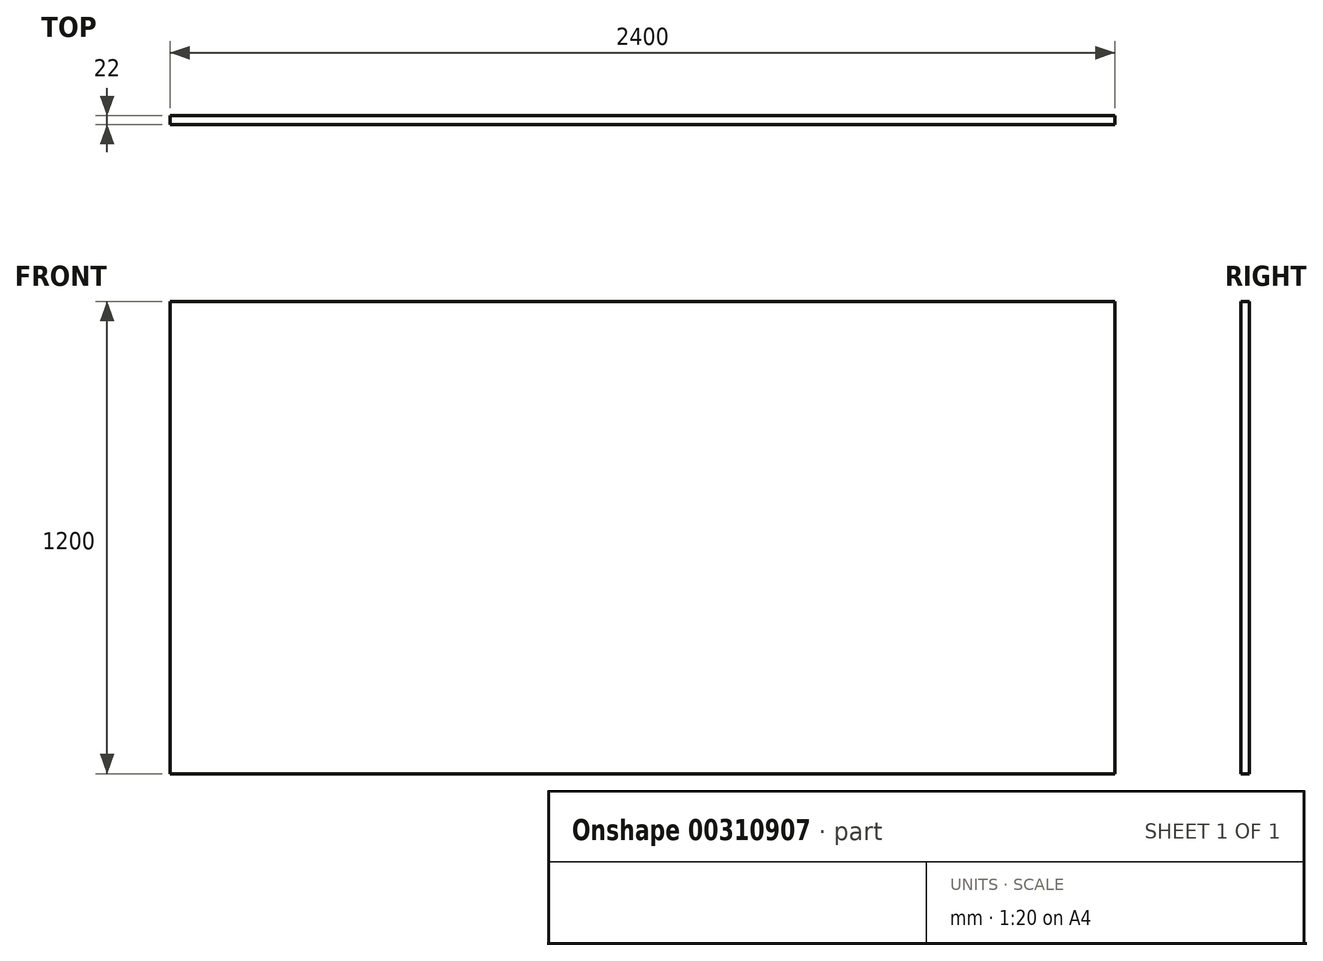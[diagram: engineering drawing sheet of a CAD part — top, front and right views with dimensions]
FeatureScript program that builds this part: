
annotation { "Feature Type Name" : "Feature", "Feature Type Description" : "" }
export const myFeature = defineFeature(function(context is Context, id is Id, definition is map)
    precondition{}
    {
        {
            var Q0;
            Q0=qCreatedBy(makeId("Front.planeOp"),FACE);
            var sketch = newSketch(context, id + "F0", { "sketchPlane" : qUnion([Q0])});
            skLineSegment(sketch, "E0.bottom", {"start": v(1200, 600) * mm, "end": v(-1200, 600) * mm});
            skLineSegment(sketch, "E0.top", {"start": v(1200, -600) * mm, "end": v(-1200, -600) * mm});
            skLineSegment(sketch, "E0.left", {"start": v(1200, 600) * mm, "end": v(1200, -600) * mm});
            skLineSegment(sketch, "E0.right", {"start": v(-1200, 600) * mm, "end": v(-1200, -600) * mm});
            skPoint(sketch, "E0.middle", {"position": v(0, 0) * mm});
            skSolve(sketch);
        }
        {
            var Q0;
            Q0=makeQuery(id+"F0.imprint","IMPRINT",FACE,{"disambiguationData":[TD([[makeQuery(id+"F0.imprint","IMPRINT",EDGE,{"derivedFrom":sQuery(id+"F0.wireOp",EDGE,"E0.bottom")}),1.0]])]});
            var Q1;
            Q1=sQuery(id+"F0.wireOp",EDGE,"E0.left");
            var Q2;
            Q2=sQuery(id+"F0.wireOp",EDGE,"E0.bottom");
            var Q3;
            Q3=sQuery(id+"F0.wireOp",EDGE,"E0.right");
            var Q4;
            Q4=sQuery(id+"F0.wireOp",EDGE,"E0.top");
            extrude(context, id + "F1", {"entities" : qUnion([Q0]), "surfaceEntities" : qUnion([Q1, Q2, Q3, Q4]), "depth" : 22 * mm});
        }
    });
